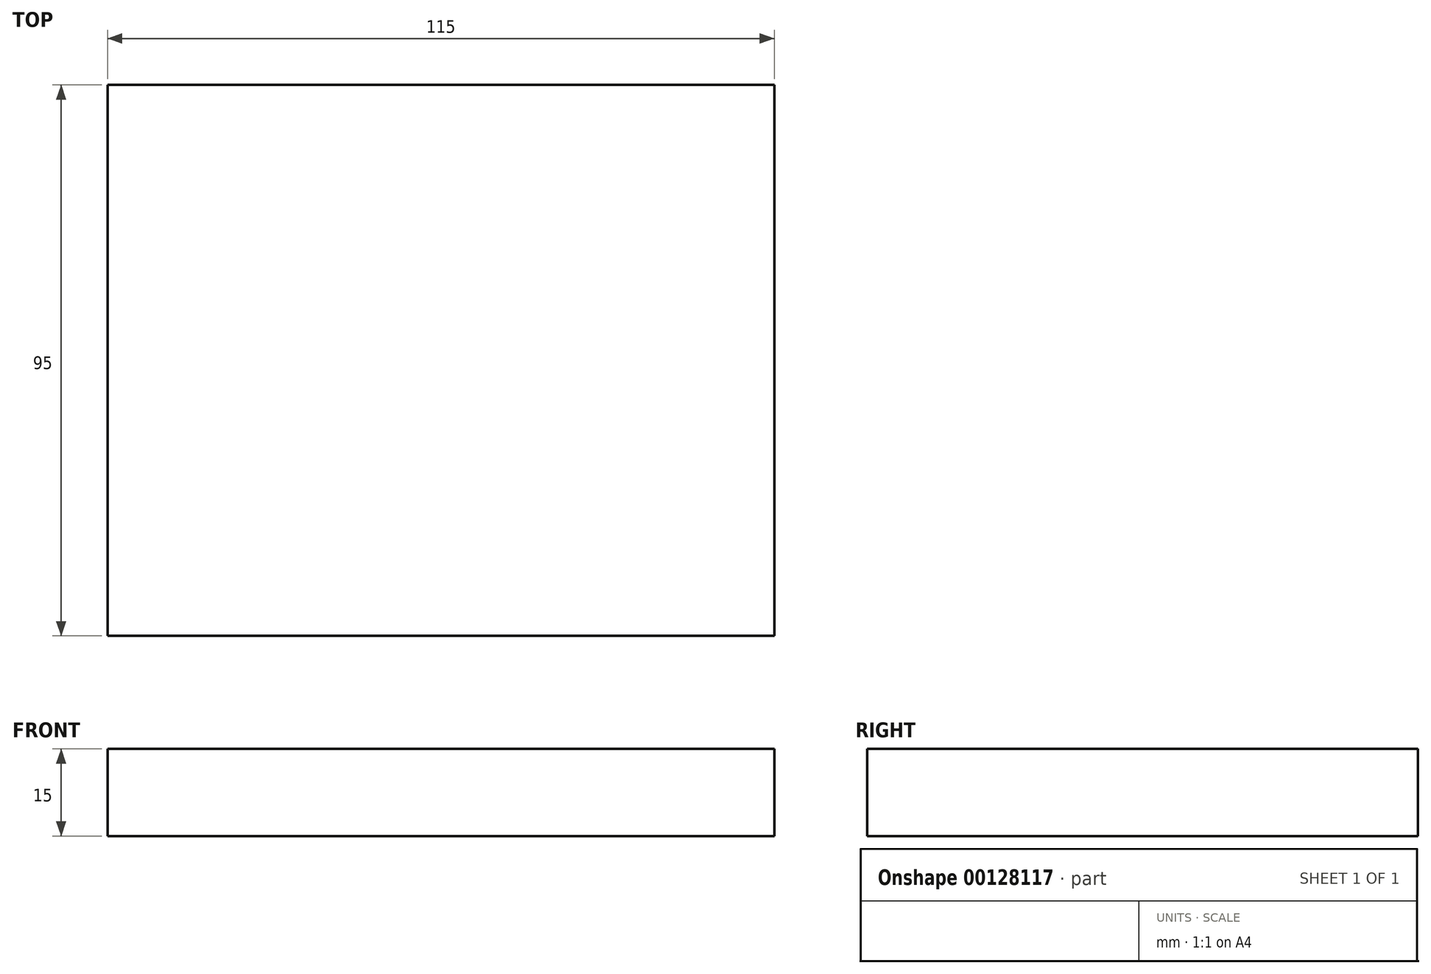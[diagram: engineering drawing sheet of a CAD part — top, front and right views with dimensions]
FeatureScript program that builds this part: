
annotation { "Feature Type Name" : "Feature", "Feature Type Description" : "" }
export const myFeature = defineFeature(function(context is Context, id is Id, definition is map)
    precondition{}
    {
        {
            var Q0;
            Q0=qCreatedBy(makeId("Top.planeOp"),FACE);
            var sketch = newSketch(context, id + "F0", { "sketchPlane" : qUnion([Q0])});
            skLineSegment(sketch, "E0.bottom", {"start": v(57.5, -47.5) * mm, "end": v(-57.5, -47.5) * mm});
            skLineSegment(sketch, "E0.top", {"start": v(57.5, 47.5) * mm, "end": v(-57.5, 47.5) * mm});
            skLineSegment(sketch, "E0.left", {"start": v(57.5, -47.5) * mm, "end": v(57.5, 47.5) * mm});
            skLineSegment(sketch, "E0.right", {"start": v(-57.5, -47.5) * mm, "end": v(-57.5, 47.5) * mm});
            skPoint(sketch, "E0.middle", {"position": v(0, 0) * mm});
            skSolve(sketch);
        }
        {
            var Q0;
            Q0 = qSketchRegion(id + "F0", true);
            extrude(context, id + "F1", {"entities" : qUnion([Q0]), "depth" : 15 * mm});
        }
    });
